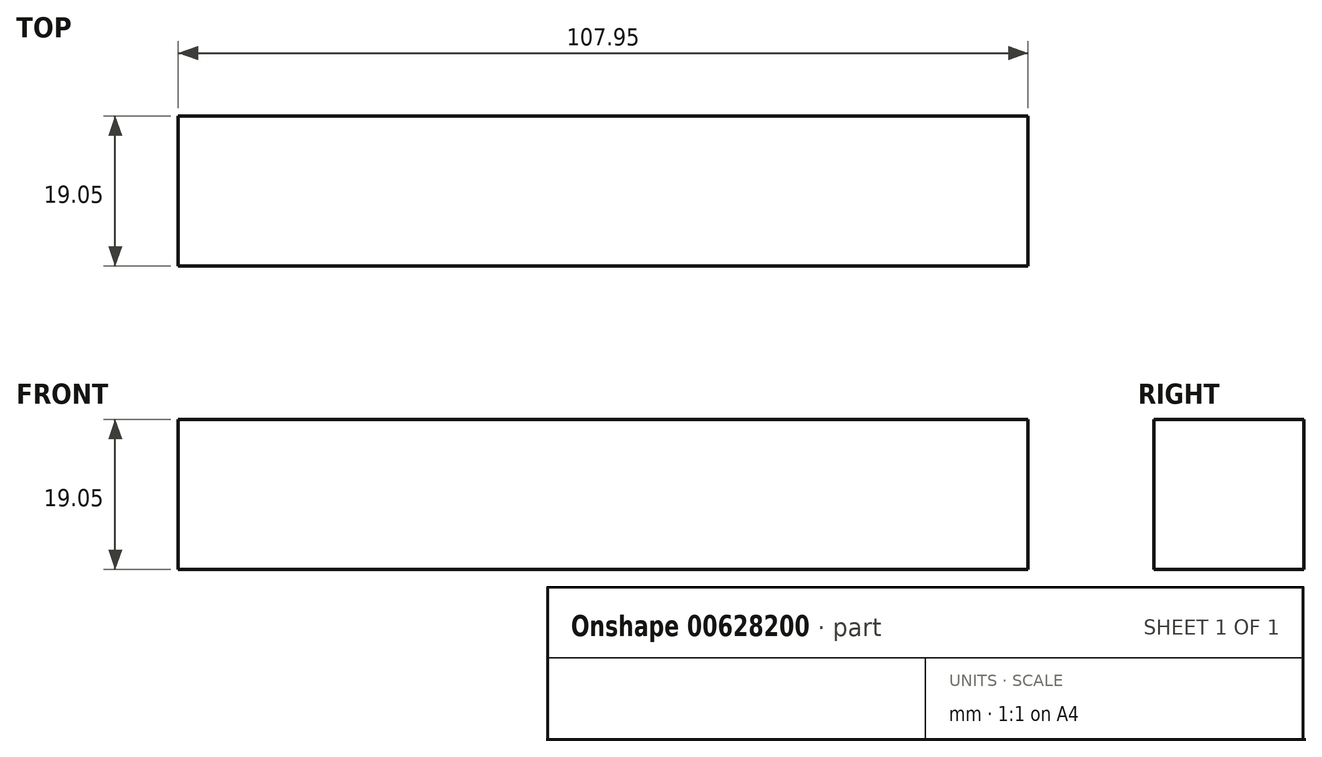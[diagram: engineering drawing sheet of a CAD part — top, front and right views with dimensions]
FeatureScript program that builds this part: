
annotation { "Feature Type Name" : "Feature", "Feature Type Description" : "" }
export const myFeature = defineFeature(function(context is Context, id is Id, definition is map)
    precondition{}
    {
        {
            var Q0;
            Q0=qCreatedBy(makeId("Front.planeOp"),FACE);
            var sketch = newSketch(context, id + "F0", { "sketchPlane" : qUnion([Q0])});
            skLineSegment(sketch, "E0.bottom", {"start": v(0, 0) * mm, "end": v(107.95, 0) * mm});
            skLineSegment(sketch, "E0.top", {"start": v(0, 19.05) * mm, "end": v(107.95, 19.05) * mm});
            skLineSegment(sketch, "E0.left", {"start": v(0, 0) * mm, "end": v(0, 19.05) * mm});
            skLineSegment(sketch, "E0.right", {"start": v(107.95, 0) * mm, "end": v(107.95, 19.05) * mm});
            skSolve(sketch);
        }
        {
            var Q0;
            Q0=qSketchRegion(id+"F0",true);
            extrude(context, id + "F1", {"entities" : qUnion([Q0]), "depth" : 19.05 * mm, "offsetDistance" : 25.4 * mm});
        }
    });
